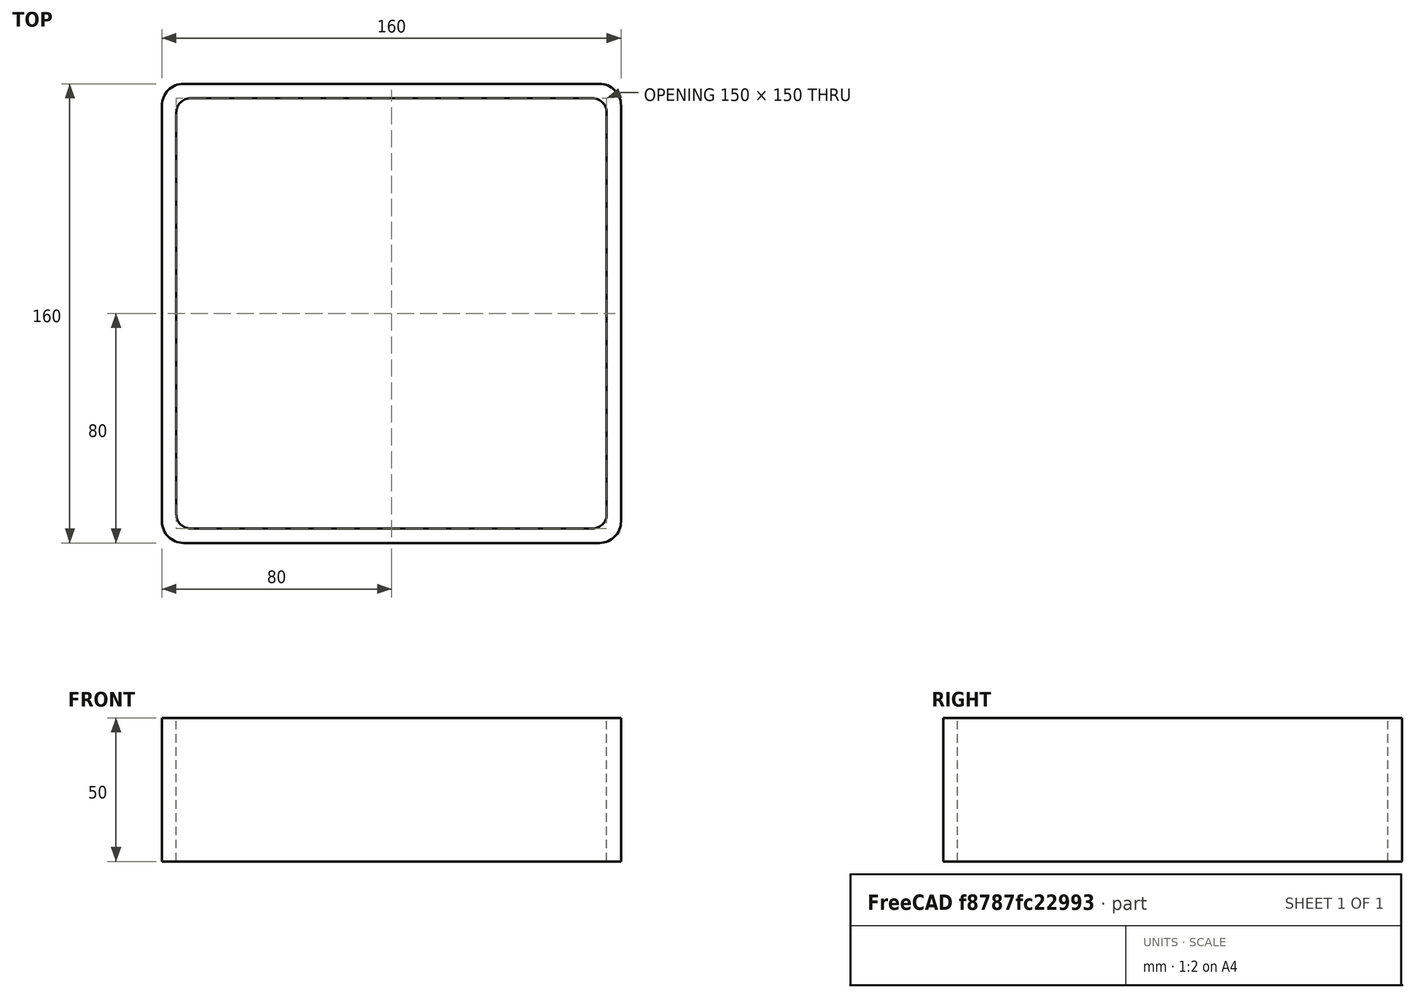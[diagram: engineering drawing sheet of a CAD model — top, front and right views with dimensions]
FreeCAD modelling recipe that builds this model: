
FCSTD DOCUMENT  (FreeCAD 0.15R4671 (Git))
Label: Square hollow section 160x160x5 EN10219 S235JRH
License: All rights reserved
LicenseURL: http://en.wikipedia.org/wiki/All_rights_reserved
objects: Sketcher::SketchObject×1, Part::Extrusion×1
note: 2 computed .brp shape members not serialized (recipe doc carries the construction recipe); baked Part::Feature solids carry a one-line shape summary decoded from their .brp

FEATURE [Sketcher::SketchObject] Sketch
  sketch-geometry (16):
    g0: LineSegment StartX=-70 StartY=75 StartZ=0 EndX=70 EndY=75 EndZ=0
    g1: LineSegment StartX=75 StartY=70 StartZ=0 EndX=75 EndY=-70 EndZ=0
    g2: LineSegment StartX=70 StartY=-75 StartZ=0 EndX=-70 EndY=-75 EndZ=0
    g3: LineSegment StartX=-75 StartY=-70 StartZ=0 EndX=-75 EndY=70 EndZ=0
    g4: LineSegment StartX=-72.5 StartY=80 StartZ=0 EndX=72.5 EndY=80 EndZ=0
    g5: LineSegment StartX=80 StartY=72.5 StartZ=0 EndX=80 EndY=-72.5 EndZ=0
    g6: LineSegment StartX=72.5 StartY=-80 StartZ=0 EndX=-72.5 EndY=-80 EndZ=0
    g7: LineSegment StartX=-80 StartY=-72.5 StartZ=0 EndX=-80 EndY=72.5 EndZ=0
    g8: ArcOfCircle CenterX=-70 CenterY=70 CenterZ=0 NormalX=0 NormalY=0 NormalZ=1 Radius=5 StartAngle=1.5708 EndAngle=3.14159
    g9: ArcOfCircle CenterX=70 CenterY=70 CenterZ=0 NormalX=0 NormalY=0 NormalZ=1 Radius=5 StartAngle=0 EndAngle=1.5708
    g10: ArcOfCircle CenterX=70 CenterY=-70 CenterZ=0 NormalX=0 NormalY=0 NormalZ=1 Radius=5 StartAngle=4.71239 EndAngle=6.28319
    g11: ArcOfCircle CenterX=-70 CenterY=-70 CenterZ=0 NormalX=0 NormalY=0 NormalZ=1 Radius=5 StartAngle=3.14159 EndAngle=4.71239
    g12: ArcOfCircle CenterX=72.5 CenterY=72.5 CenterZ=0 NormalX=0 NormalY=0 NormalZ=1 Radius=7.5 StartAngle=0 EndAngle=1.5708
    g13: ArcOfCircle CenterX=72.5 CenterY=-72.5 CenterZ=0 NormalX=0 NormalY=0 NormalZ=1 Radius=7.5 StartAngle=4.71239 EndAngle=6.28319
    g14: ArcOfCircle CenterX=-72.5 CenterY=-72.5 CenterZ=0 NormalX=0 NormalY=0 NormalZ=1 Radius=7.5 StartAngle=3.14159 EndAngle=4.71239
    g15: ArcOfCircle CenterX=-72.5 CenterY=72.5 CenterZ=0 NormalX=0 NormalY=0 NormalZ=1 Radius=7.5 StartAngle=1.5708 EndAngle=3.14159
  constraints (36):
    c: Horizontal(g2)
    c: Vertical(g3)
    c: Horizontal(g6)
    c: Vertical(g7)
    c: Tangent(g3,g8) = 1.5708
    c: Tangent(g0,g8) = 1.5708
    c: Tangent(g0,g9) = 1.5708
    c: Tangent(g1,g9) = 1.5708
    c: Tangent(g1,g10) = 1.5708
    c: Tangent(g2,g10) = 1.5708
    c: Tangent(g2,g11) = 1.5708
    c: Tangent(g3,g11) = 1.5708
    c: Tangent(g4,g12) = 1.5708
    c: Tangent(g5,g12) = 1.5708
    c: Tangent(g5,g13) = 1.5708
    c: Tangent(g6,g13) = 1.5708
    c: Tangent(g6,g14) = 1.5708
    c: Tangent(g7,g14) = 1.5708
    c: Tangent(g7,g15) = 1.5708
    c: Tangent(g4,g15) = 1.5708
    c: Equal(g9,g8)
    c: Equal(g9,g11)
    c: Equal(g9,g10)
    c: Equal(g12,g15)
    c: Equal(g12,g14)
    c: Equal(g12,g13)
    c: Symmetric(g4,g6,g-1)
    c: Symmetric(g7,g5,g-2)
    c: DistanceY(g4,g6) = -160
    c: DistanceX(g7,g5) = 160
    c: Symmetric(g3,g1,g-2)
    c: Symmetric(g0,g2,g-1)
    c: DistanceY(g0,g4) = 5
    c: DistanceX(g5,g1) = -5
    c: Radius(g9) = 5
    c: Radius(g12) = 7.5
FEATURE [Part::Extrusion] Extrude  label="Square hollow section 160x160x5 EN10219 S235JRH"
  Base = -> Sketch
  Dir = (0,0,50)
  Solid = true
